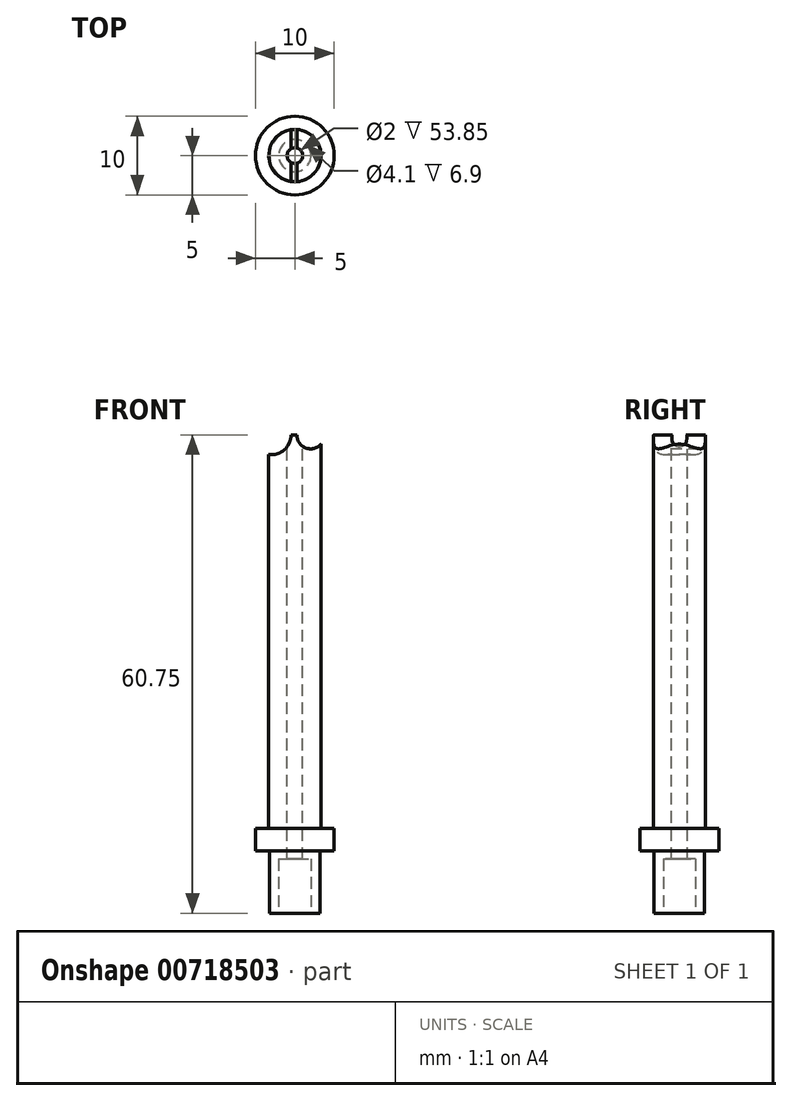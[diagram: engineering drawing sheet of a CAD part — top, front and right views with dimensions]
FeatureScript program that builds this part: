
annotation { "Feature Type Name" : "Feature", "Feature Type Description" : "" }
export const myFeature = defineFeature(function(context is Context, id is Id, definition is map)
    precondition{}
    {
        {
            var Q0;
            Q0=qCreatedBy(makeId("Top.planeOp"),FACE);
            var sketch = newSketch(context, id + "F0", { "sketchPlane" : qUnion([Q0])});
            skCircle(sketch, "E0", {"center": v(0, 0) * mm, "radius": 3.33 * mm});
            skSolve(sketch);
        }
        {
            var Q0;
            Q0=makeQuery(id+"F0.imprint","IMPRINT",FACE,{"disambiguationData":[TD([[makeQuery(id+"F0.imprint","IMPRINT",EDGE,{"derivedFrom":sQuery(id+"F0.wireOp",EDGE,"E0")}),1.0]])]});
            extrude(context, id + "F1", {"entities" : qUnion([Q0]), "depth" : 50 * mm, "offsetDistance" : 25 * mm});
        }
        {
            var Q0;
            Q0=makeQuery(id+"F0.imprint","IMPRINT",FACE,{"disambiguationData":[TD([[makeQuery(id+"F0.imprint","IMPRINT",EDGE,{"derivedFrom":sQuery(id+"F0.wireOp",EDGE,"E0")}),1.0]])]});
            var sketch = newSketch(context, id + "F2", { "sketchPlane" : qUnion([Q0])});
            skCircle(sketch, "E1", {"center": v(0, 0) * mm, "radius": 5 * mm});
            skSolve(sketch);
        }
        {
            var Q0;
            Q0 = qSketchRegion(id + "F2", true);
            var Q1;
            Q1=makeQuery(id+"F2.imprint","IMPRINT",FACE,{"disambiguationData":[TD([[makeQuery(id+"F2.imprint","IMPRINT",EDGE,{"derivedFrom":sQuery(id+"F2.wireOp",EDGE,"E1")}),1.0]])]});
            extrude(context, id + "F3", {"entities" : qUnion([Q0, Q1]), "operationType" : NewBodyOperationType.ADD, "oppositeDirection" : true, "depth" : 2.85 * mm, "offsetDistance" : 25 * mm});
        }
        {
            var Q0;
            Q0=makeQuery(id+"F3.opExtrude","CAP_FACE",FACE,{"disambiguationData":[OSD([sQuery(id+"F2.wireOp",EDGE,"E1")])],"isStart":false});
            var sketch = newSketch(context, id + "F4", { "sketchPlane" : qUnion([Q0])});
            skCircle(sketch, "E2", {"center": v(0, 0) * mm, "radius": 3.2 * mm});
            skSolve(sketch);
        }
        {
            var Q0;
            Q0=makeQuery(id+"F4.imprint","IMPRINT",FACE,{"disambiguationData":[TD([[makeQuery(id+"F4.imprint","IMPRINT",EDGE,{"derivedFrom":sQuery(id+"F4.wireOp",EDGE,"E2")}),1.0]])]});
            extrude(context, id + "F5", {"entities" : qUnion([Q0]), "operationType" : NewBodyOperationType.ADD, "depth" : 7.9 * mm, "offsetDistance" : 25 * mm});
        }
        {
            var Q0;
            Q0=makeQuery(id+"F1.opExtrude","CAP_FACE",FACE,{"disambiguationData":[OSD([sQuery(id+"F0.wireOp",EDGE,"E0")])],"isStart":false});
            var sketch = newSketch(context, id + "F6", { "sketchPlane" : qUnion([Q0])});
            skCircle(sketch, "E3", {"center": v(0, 0) * mm, "radius": 1 * mm});
            skSolve(sketch);
        }
        {
            var Q0;
            Q0=makeQuery(id+"F6.imprint","IMPRINT",FACE,{"disambiguationData":[TD([[makeQuery(id+"F6.imprint","IMPRINT",EDGE,{"derivedFrom":sQuery(id+"F6.wireOp",EDGE,"E3")}),1.0]])]});
            extrude(context, id + "F7", {"entities" : qUnion([Q0]), "operationType" : NewBodyOperationType.REMOVE, "oppositeDirection" : true, "depth" : 55 * mm, "offsetDistance" : 25 * mm});
        }
        {
            var Q0;
            Q0=makeQuery(id+"F5.opExtrude","CAP_FACE",FACE,{"disambiguationData":[OSD([sQuery(id+"F4.wireOp",EDGE,"E2")])],"isStart":false});
            var sketch = newSketch(context, id + "F8", { "sketchPlane" : qUnion([Q0])});
            skCircle(sketch, "E4", {"center": v(0, 0) * mm, "radius": 2.05 * mm});
            skSolve(sketch);
        }
        {
            var Q0;
            Q0=makeQuery(id+"F8.imprint","IMPRINT",FACE,{"disambiguationData":[TD([[makeQuery(id+"F8.imprint","IMPRINT",EDGE,{"derivedFrom":sQuery(id+"F8.wireOp",EDGE,"E4")}),1.0]])]});
            extrude(context, id + "F9", {"entities" : qUnion([Q0]), "operationType" : NewBodyOperationType.REMOVE, "oppositeDirection" : true, "depth" : 6.9 * mm, "offsetDistance" : 25 * mm});
        }
        {
            var Q0;
            Q0=qCreatedBy(makeId("Front.planeOp"),FACE);
            var sketch = newSketch(context, id + "F10", { "sketchPlane" : qUnion([Q0])});
            skCircle(sketch, "E5", {"center": v(2, 50) * mm, "radius": 1.75 * mm});
            skCircle(sketch, "E6", {"center": v(-3, 50) * mm, "radius": 2.5 * mm});
            skSolve(sketch);
        }
        {
            var Q0;
            Q0=makeQuery(id+"F10.imprint","IMPRINT",FACE,{"disambiguationData":[TD([[makeQuery(id+"F10.imprint","IMPRINT",EDGE,{"derivedFrom":sQuery(id+"F10.wireOp",EDGE,"E6")}),1.0]])]});
            var Q1;
            Q1=makeQuery(id+"F10.imprint","IMPRINT",FACE,{"disambiguationData":[TD([[makeQuery(id+"F10.imprint","IMPRINT",EDGE,{"derivedFrom":sQuery(id+"F10.wireOp",EDGE,"E5")}),1.0]])]});
            extrude(context, id + "F11", {"entities" : qUnion([Q0, Q1]), "operationType" : NewBodyOperationType.REMOVE, "endBound" : BoundingType.SYMMETRIC, "oppositeDirection" : true, "depth" : 8 * mm, "offsetDistance" : 25 * mm});
        }
    });
